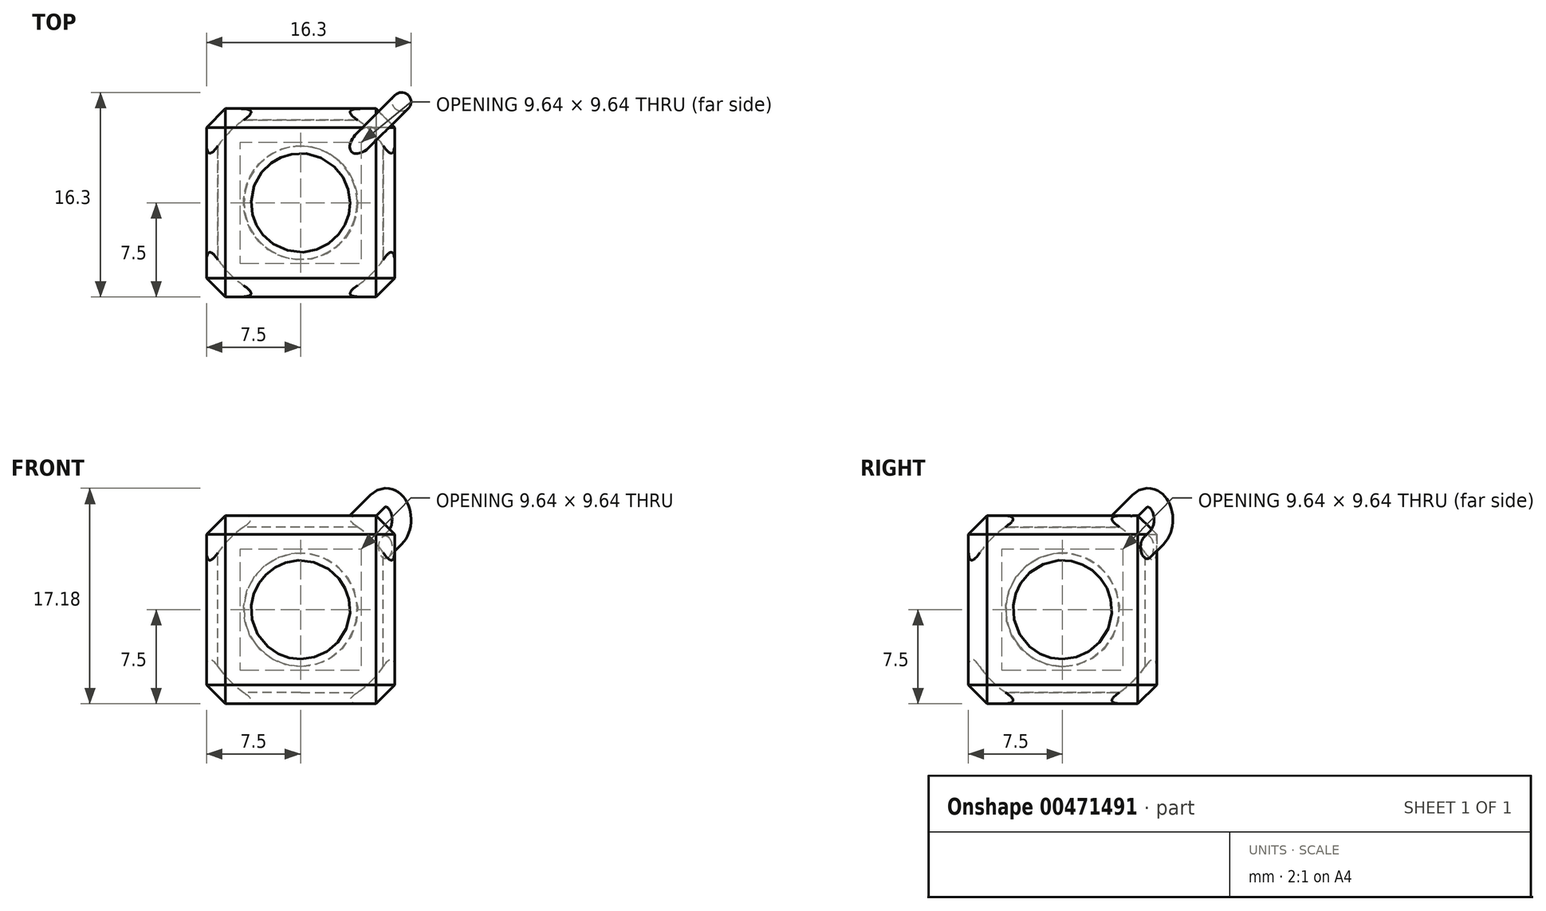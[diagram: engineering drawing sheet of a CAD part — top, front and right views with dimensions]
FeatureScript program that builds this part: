
annotation { "Feature Type Name" : "Feature", "Feature Type Description" : "" }
export const myFeature = defineFeature(function(context is Context, id is Id, definition is map)
    precondition{}
    {
        {
            assignVariable(context, id + "F0", {"name" : "size", "anyValue" : 15});
        }
        {
            var Q0;
            Q0=qCreatedBy(makeId("Front.planeOp"),FACE);
            var sketch = newSketch(context, id + "F1", { "sketchPlane" : qUnion([Q0])});
            skLineSegment(sketch, "E0.bottom", {"start": v(-7.5, 7.5) * mm, "end": v(7.5, 7.5) * mm});
            skLineSegment(sketch, "E0.top", {"start": v(-7.5, -7.5) * mm, "end": v(7.5, -7.5) * mm});
            skLineSegment(sketch, "E0.left", {"start": v(-7.5, 7.5) * mm, "end": v(-7.5, -7.5) * mm});
            skLineSegment(sketch, "E0.right", {"start": v(7.5, 7.5) * mm, "end": v(7.5, -7.5) * mm});
            skLineSegment(sketch, "E1", {"start": v(0, 7.5) * mm, "end": v(0, -7.5) * mm, "construction": true});
            skLineSegment(sketch, "E2", {"start": v(-7.5, 0) * mm, "end": v(7.5, 0) * mm, "construction": true});
            skSolve(sketch);
        }
        {
            var Q0;
            Q0 = qSketchRegion(id + "F1", true);
            extrude(context, id + "F2", {"entities" : qUnion([Q0]), "endBound" : BoundingType.SYMMETRIC, "depth" : (getVariable(context, 'size')) * mm});
        }
        {
            var Q0;
            Q0=qCreatedBy(makeId("Top.planeOp"),FACE);
            var sketch = newSketch(context, id + "F3", { "sketchPlane" : qUnion([Q0])});
            skArc(sketch, "E3", {"start": v(0, -8) * mm, "mid": v(8, 0) * mm, "end": v(0, 8) * mm});
            skLineSegment(sketch, "E4", {"start": v(0, 8) * mm, "end": v(0, -8) * mm});
            skSolve(sketch);
        }
        {
            var Q0;
            Q0=makeQuery(id+"F3.imprint","IMPRINT",FACE,{"disambiguationData":[TD([[makeQuery(id+"F3.imprint","IMPRINT",EDGE,{"derivedFrom":sQuery(id+"F3.wireOp",EDGE,"E3")}),1.0]])]});
            var Q1;
            Q1=sQuery(id+"F3.wireOp",EDGE,"E3");
            var Q2;
            Q2=sQuery(id+"F3.wireOp",EDGE,"E4");
            revolve(context, id + "F4", {"operationType" : NewBodyOperationType.REMOVE, "entities" : qUnion([Q0]), "surfaceEntities" : qUnion([Q1]), "axis" : qUnion([Q2]), "revolveType" : RevolveType.FULL});
        }
        {
            var Q0;
            Q0=makeQuery(id+"F2.opExtrude","SWEPT_EDGE",EDGE,{"disambiguationData":[OSD([sQuery(id+"F1.wireOp",EDGE,"E0.top"),sQuery(id+"F1.wireOp",EDGE,"E0.left")])]});
            var Q1;
            Q1=makeQuery(id+"F2.opExtrude","CAP_EDGE",EDGE,{"disambiguationData":[OSD([sQuery(id+"F1.wireOp",EDGE,"E0.top")])],"isStart":true});
            var Q2;
            Q2=makeQuery(id+"F2.opExtrude","CAP_EDGE",EDGE,{"disambiguationData":[OSD([sQuery(id+"F1.wireOp",EDGE,"E0.top")])],"isStart":false});
            var Q3;
            Q3=makeQuery(id+"F2.opExtrude","SWEPT_EDGE",EDGE,{"disambiguationData":[OSD([sQuery(id+"F1.wireOp",EDGE,"E0.top"),sQuery(id+"F1.wireOp",EDGE,"E0.right")])]});
            var Q4;
            Q4=makeQuery(id+"F2.opExtrude","CAP_EDGE",EDGE,{"disambiguationData":[OSD([sQuery(id+"F1.wireOp",EDGE,"E0.right")])],"isStart":false});
            var Q5;
            Q5=makeQuery(id+"F2.opExtrude","CAP_EDGE",EDGE,{"disambiguationData":[OSD([sQuery(id+"F1.wireOp",EDGE,"E0.left")])],"isStart":false});
            var Q6;
            Q6=makeQuery(id+"F2.opExtrude","CAP_EDGE",EDGE,{"disambiguationData":[OSD([sQuery(id+"F1.wireOp",EDGE,"E0.bottom")])],"isStart":false});
            var Q7;
            Q7=makeQuery(id+"F2.opExtrude","SWEPT_EDGE",EDGE,{"disambiguationData":[OSD([sQuery(id+"F1.wireOp",EDGE,"E0.bottom"),sQuery(id+"F1.wireOp",EDGE,"E0.left")])]});
            var Q8;
            Q8=makeQuery(id+"F2.opExtrude","CAP_EDGE",EDGE,{"disambiguationData":[OSD([sQuery(id+"F1.wireOp",EDGE,"E0.left")])],"isStart":true});
            var Q9;
            Q9=makeQuery(id+"F2.opExtrude","CAP_EDGE",EDGE,{"disambiguationData":[OSD([sQuery(id+"F1.wireOp",EDGE,"E0.bottom")])],"isStart":true});
            var Q10;
            Q10=makeQuery(id+"F2.opExtrude","CAP_EDGE",EDGE,{"disambiguationData":[OSD([sQuery(id+"F1.wireOp",EDGE,"E0.right")])],"isStart":true});
            var Q11;
            Q11=makeQuery(id+"F2.opExtrude","SWEPT_EDGE",EDGE,{"disambiguationData":[OSD([sQuery(id+"F1.wireOp",EDGE,"E0.bottom"),sQuery(id+"F1.wireOp",EDGE,"E0.right")])]});
            chamfer(context, id + "F5", {"entities" : qUnion([Q0, Q1, Q2, Q3, Q4, Q5, Q6, Q7, Q8, Q9, Q10, Q11]), "width" : 1.5 * mm, "tangentPropagation" : true});
        }
        {
            var Q0;
            Q0=makeQuery(id+"F4.boolean.opBoolean","INTERSECT",EDGE,{"derivedFrom":[makeQuery(id+"F2.opExtrude","SWEPT_FACE",FACE,{"disambiguationData":[OSD([sQuery(id+"F1.wireOp",EDGE,"E0.top")])]}),makeQuery(id+"F4.opRevolve","SWEPT_FACE",FACE,{"disambiguationData":[OSD([sQuery(id+"F3.wireOp",EDGE,"E3")])]})]});
            var Q1;
            Q1=makeQuery(id+"F4.boolean.opBoolean","INTERSECT",EDGE,{"derivedFrom":[makeQuery(id+"F2.opExtrude","SWEPT_FACE",FACE,{"disambiguationData":[OSD([sQuery(id+"F1.wireOp",EDGE,"E0.left")])]}),makeQuery(id+"F4.opRevolve","SWEPT_FACE",FACE,{"disambiguationData":[OSD([sQuery(id+"F3.wireOp",EDGE,"E3")])]})]});
            var Q2;
            Q2=makeQuery(id+"F4.boolean.opBoolean","INTERSECT",EDGE,{"derivedFrom":[makeQuery(id+"F2.opExtrude","CAP_FACE",FACE,{"disambiguationData":[OSD([sQuery(id+"F1.wireOp",EDGE,"E0.bottom"),sQuery(id+"F1.wireOp",EDGE,"E0.top"),sQuery(id+"F1.wireOp",EDGE,"E0.left"),sQuery(id+"F1.wireOp",EDGE,"E0.right")])],"isStart":false}),makeQuery(id+"F4.opRevolve","SWEPT_FACE",FACE,{"disambiguationData":[OSD([sQuery(id+"F3.wireOp",EDGE,"E3")])]})]});
            var Q3;
            Q3=makeQuery(id+"F4.boolean.opBoolean","INTERSECT",EDGE,{"derivedFrom":[makeQuery(id+"F2.opExtrude","SWEPT_FACE",FACE,{"disambiguationData":[OSD([sQuery(id+"F1.wireOp",EDGE,"E0.right")])]}),makeQuery(id+"F4.opRevolve","SWEPT_FACE",FACE,{"disambiguationData":[OSD([sQuery(id+"F3.wireOp",EDGE,"E3")])]})]});
            var Q4;
            Q4=makeQuery(id+"F4.boolean.opBoolean","INTERSECT",EDGE,{"derivedFrom":[makeQuery(id+"F2.opExtrude","SWEPT_FACE",FACE,{"disambiguationData":[OSD([sQuery(id+"F1.wireOp",EDGE,"E0.bottom")])]}),makeQuery(id+"F4.opRevolve","SWEPT_FACE",FACE,{"disambiguationData":[OSD([sQuery(id+"F3.wireOp",EDGE,"E3")])]})]});
            var Q5;
            Q5=makeQuery(id+"F4.boolean.opBoolean","INTERSECT",EDGE,{"derivedFrom":[makeQuery(id+"F2.opExtrude","CAP_FACE",FACE,{"disambiguationData":[OSD([sQuery(id+"F1.wireOp",EDGE,"E0.bottom"),sQuery(id+"F1.wireOp",EDGE,"E0.top"),sQuery(id+"F1.wireOp",EDGE,"E0.left"),sQuery(id+"F1.wireOp",EDGE,"E0.right")])],"isStart":true}),makeQuery(id+"F4.opRevolve","SWEPT_FACE",FACE,{"disambiguationData":[OSD([sQuery(id+"F3.wireOp",EDGE,"E3")])]})]});
            fillet(context, id + "F6", {"entities" : qUnion([Q0, Q1, Q2, Q3, Q4, Q5]), "radius" : 0.5 * mm, "tangentPropagation" : true, "rho" : 0.5, "crossSection" : FilletCrossSection.CONIC, "allowEdgeOverflow" : false});
        }
        {
            var Q0;
            Q0=qCreatedBy(makeId("Front.planeOp"),FACE);
            var sketch = newSketch(context, id + "F7", { "sketchPlane" : qUnion([Q0])});
            skArc(sketch, "E5", {"start": v(0, -4.5) * mm, "mid": v(4.5, 0) * mm, "end": v(0, 4.5) * mm});
            skLineSegment(sketch, "E6", {"start": v(0, 4.5) * mm, "end": v(0, -4.5) * mm});
            skSolve(sketch);
        }
        {
            var Q0;
            Q0=makeQuery(id+"F7.imprint","IMPRINT",FACE,{"disambiguationData":[TD([[makeQuery(id+"F7.imprint","IMPRINT",EDGE,{"derivedFrom":sQuery(id+"F7.wireOp",EDGE,"E5")}),1.0]])]});
            var Q1;
            Q1=sQuery(id+"F7.wireOp",EDGE,"E6");
            revolve(context, id + "F8", {"entities" : qUnion([Q0]), "axis" : qUnion([Q1]), "revolveType" : RevolveType.FULL});
        }
        {
            var Q0;
            {var subQ0=sQuery(id+"F1.wireOp",EDGE,"E0.top");var subQ1=sQuery(id+"F1.wireOp",EDGE,"E0.right");Q0=makeQuery(id+"F5.opChamfer","BLEND_VERTEX",VERTEX,{"blendedFrom":[makeQuery(id+"F2.opExtrude","CAP_VERTEX",VERTEX,{"disambiguationData":[OSD([subQ0,subQ1])],"isStart":true}),makeQuery(id+"F2.opExtrude","SWEPT_EDGE",EDGE,{"disambiguationData":[OSD([subQ0,subQ1])]}),makeQuery(id+"F2.opExtrude","CAP_EDGE",EDGE,{"disambiguationData":[OSD([subQ0])],"isStart":true}),makeQuery(id+"F2.opExtrude","SWEPT_FACE",FACE,{"disambiguationData":[OSD([subQ0])]})],"blendedInto":[makeQuery(id+"F2.opExtrude","SWEPT_FACE",FACE,{"disambiguationData":[OSD([subQ0])]})]});}
            var Q1;
            {var subQ0=sQuery(id+"F1.wireOp",EDGE,"E0.bottom");var subQ1=sQuery(id+"F1.wireOp",EDGE,"E0.left");Q1=makeQuery(id+"F5.opChamfer","BLEND_VERTEX",VERTEX,{"blendedFrom":[makeQuery(id+"F2.opExtrude","CAP_VERTEX",VERTEX,{"disambiguationData":[OSD([subQ0,subQ1])],"isStart":false}),makeQuery(id+"F2.opExtrude","SWEPT_EDGE",EDGE,{"disambiguationData":[OSD([subQ0,subQ1])]}),makeQuery(id+"F2.opExtrude","CAP_EDGE",EDGE,{"disambiguationData":[OSD([subQ0])],"isStart":false}),makeQuery(id+"F2.opExtrude","SWEPT_FACE",FACE,{"disambiguationData":[OSD([subQ0])]})],"blendedInto":[makeQuery(id+"F2.opExtrude","SWEPT_FACE",FACE,{"disambiguationData":[OSD([subQ0])]})]});}
            var Q2;
            {var subQ0=sQuery(id+"F1.wireOp",EDGE,"E0.bottom");var subQ1=sQuery(id+"F1.wireOp",EDGE,"E0.right");Q2=makeQuery(id+"F5.opChamfer","BLEND_VERTEX",VERTEX,{"blendedFrom":[makeQuery(id+"F2.opExtrude","CAP_VERTEX",VERTEX,{"disambiguationData":[OSD([subQ0,subQ1])],"isStart":true}),makeQuery(id+"F2.opExtrude","SWEPT_EDGE",EDGE,{"disambiguationData":[OSD([subQ0,subQ1])]}),makeQuery(id+"F2.opExtrude","CAP_EDGE",EDGE,{"disambiguationData":[OSD([subQ0])],"isStart":true}),makeQuery(id+"F2.opExtrude","SWEPT_FACE",FACE,{"disambiguationData":[OSD([subQ0])]})],"blendedInto":[makeQuery(id+"F2.opExtrude","SWEPT_FACE",FACE,{"disambiguationData":[OSD([subQ0])]})]});}
            cPlane(context, id + "F9", {"entities" : qUnion([Q0, Q1, Q2]), "cplaneType" : CPlaneType.THREE_POINT, "offset" : 25 * mm, "width" : 150 * mm, "height" : 150 * mm});
        }
        {
            var Q0;
            Q0=qCreatedBy(id+"F9.planeOp",FACE);
            var sketch = newSketch(context, id + "F10", { "sketchPlane" : qUnion([Q0])});
            skLineSegment(sketch, "E7", {"start": v(8, 8.18) * mm, "end": v(8.62, 8.61) * mm});
            skLineSegment(sketch, "E8", {"start": v(10.03, 5.32) * mm, "end": v(10.64, 5.75) * mm});
            skArc(sketch, "E9", {"start": v(10.64, 5.75) * mm, "mid": v(11.06, 8.2) * mm, "end": v(8.62, 8.61) * mm});
            skLineSegment(sketch, "E10", {"start": v(8.62, 8.61) * mm, "end": v(10.64, 5.75) * mm, "construction": true});
            skLineSegment(sketch, "E11", {"start": v(8, 8.18) * mm, "end": v(10.03, 5.32) * mm, "construction": true});
            skLineSegment(sketch, "E12", {"start": v(8.49, 7.5) * mm, "end": v(8, 8.18) * mm, "construction": true});
            skLineSegment(sketch, "E13", {"start": v(9.55, 6) * mm, "end": v(10.03, 5.32) * mm, "construction": true});
            skSolve(sketch);
        }
        {
            var Q0;
            {var subQ0=sQuery(id+"F1.wireOp",EDGE,"E0.right");var subQ1=sQuery(id+"F1.wireOp",EDGE,"E0.bottom");Q0=makeQuery(id+"F5.opChamfer","BLEND_FACE",FACE,{"disambiguationData":[OSD([subQ1,subQ0]),TDD([makeQuery(id+"F2.opExtrude","CAP_VERTEX",VERTEX,{"disambiguationData":[OSD([subQ1,subQ0])],"isStart":true})])]});}
            var sketch = newSketch(context, id + "F11", { "sketchPlane" : qUnion([Q0])});
            skCircle(sketch, "E14", {"center": v(1.03, 1.78) * mm, "radius": 0.75 * mm});
            skSolve(sketch);
        }
        {
            var Q0;
            Q0 = qSketchRegion(id + "F11", true);
            var Q1;
            Q1=sQuery(id+"F10.wireOp",EDGE,"ZcKcVCXd-u47N-qY5P-52to-HqSAMtr9PRpy");
            var Q2;
            Q2=sQuery(id+"F10.wireOp",EDGE,"E9");
            var Q3;
            Q3=sQuery(id+"F10.wireOp",EDGE,"E7");
            var Q4;
            Q4=sQuery(id+"F10.wireOp",EDGE,"E8");
            sweep(context, id + "F12", {"operationType" : NewBodyOperationType.ADD, "profiles" : qUnion([Q0]), "surfaceProfiles" : qUnion([Q1]), "path" : qUnion([Q2, Q3, Q4])});
        }
        {
            var Q0;
            Q0=makeQuery(id+"F12.opSweep","CAP_FACE",FACE,{"disambiguationData":[OSD([sQuery(id+"F10.wireOp",VERTEX,"ZcKcVCXd-u47N-qY5P-52to-HqSAMtr9PRpy.start"),sQuery(id+"F11.wireOp",EDGE,"E14")])],"isStart":true});
            extrude(context, id + "F13", {"entities" : qUnion([Q0]), "operationType" : NewBodyOperationType.ADD, "endBound" : BoundingType.UP_TO_NEXT, "depth" : 25 * mm});
        }
        {
            var Q0;
            Q0=makeQuery(id+"F12.opSweep","CAP_FACE",FACE,{"disambiguationData":[OSD([sQuery(id+"F10.wireOp",VERTEX,"ZcKcVCXd-u47N-qY5P-52to-HqSAMtr9PRpy.end"),sQuery(id+"F11.wireOp",EDGE,"E14")])],"isStart":false});
            extrude(context, id + "F14", {"entities" : qUnion([Q0]), "operationType" : NewBodyOperationType.ADD, "endBound" : BoundingType.UP_TO_NEXT, "depth" : 25 * mm});
        }
    });
